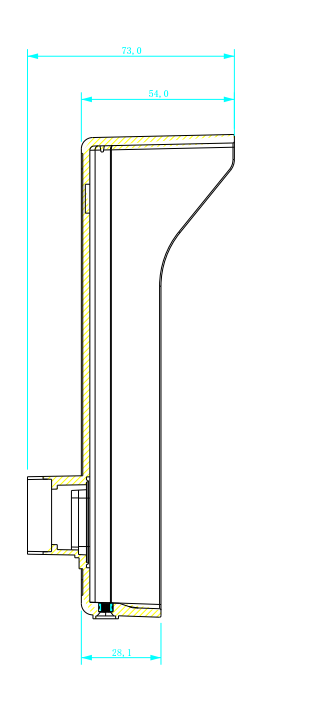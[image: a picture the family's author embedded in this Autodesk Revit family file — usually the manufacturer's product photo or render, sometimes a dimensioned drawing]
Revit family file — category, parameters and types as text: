
# Revit family: CR-02BD
name_source: partatom
category: Устройства связи
units: mm (PartAtom-declared; Revit-internal decimal feet)

## family parameters
Всегда вертикально = Нет
На основе рабочей плоскости = Да
Общий = Да
При загрузке вырезать с полостями = Нет
Размер круглого соединителя = Использовать диаметр
Сохранять ориентацию аннотаций = Нет
Тип детали = Нормальный
Точка принадлежности помещению = Нет

## types (1)
- CR-02BD
    ADSK_URL документации изделия = -
    ADSK_URL страницы изделия = https://www.bas-ip.ru
    ADSK_Версия Revit = Revit 2020
    ADSK_Единица измерения = шт
    ADSK_Завод-изготовитель = BAS-IP
    ADSK_Классификация нагрузок = Считыватель со встроенным контроллером
    ADSK_Количество фаз = 1
    ADSK_Коэффициент мощности = 0.9
    ADSK_Марка = CR-02BD
    ADSK_Наименование = Считыватель со встроенным контроллером CR-02BD
    ADSK_Наименование краткое = CR-02BD
    ADSK_Напряжение = 12 В
    ADSK_Номинальная мощность = 6 Вт
    ADSK_Полная мощность = 6 В·А
    ADSK_Размер_Длина = 159 мм
    ADSK_Размер_Толщина = 48 мм
    ADSK_Размер_Ширина = 99 мм
    BIM library = https://bimlib.ru
    URL = https://www.bas-ip.ru
    Возможность подключения дополнительного считывателя = Нет
    Группа модели = Считыватель со встроенным контроллером CR-02BD
    Допустимая влажность при эксплуатации = до 93%
    Звуковой сигнал открытия двери = Есть
    Изготовитель = BAS-IP
    Изображение типоразмера = <Нет>
    Интеграция со СКУД = Выход WIEGAND-26, 32, 34, 37, 40, 42, 56, 58, 64 бит
    Интерфейс подключения для ПО управления, ПО учета и статистики и ПО конфигурирования = RJ45 Ethernet
    Используемые протоколы работы в сети Ethernet = TCP/IP
    Класс защищенности = IP65
    Количество идентификаторов в памяти панели = 20 000
    Количество карт администратора = 1
    Корпус = Металлический сплав с высоким уровнем антивандальности и коррозионной стойкости (На лицевой панели – пластиковая декоративная накладка)
    Материал корпуса = Материал серый
    Описание = Считыватель со встроенным контроллером CR-02BD - Внешний сетевой считыватель бесконтактных карт и брелоков со встроенным контроллером и поддержкой технологии UKEY: считывание карт, брелоков и мобильных идентификаторов по стандартам Mifare® Plus и Mifare® Classic, Bluetooth, NFC. С помощью внешнего сетевого считывателя бесконтактных карт BAS-IP CR-02BD можно считывать бесконтактные карты, брелоки, а также мобильные идентификаторы с мобильных устройств
    Отметка по умолчанию = 0 мм
    Питание = PoE, +12 В (+12% -6%)
    Подключение датчика двери = Есть
    Подключение кнопки выхода = Есть
    Потребление питания = 6,0 Вт, в режиме ожидания – 2,5 Вт
    Размер = 99×159×48 мм
    Размер кронштейна = 94x 156x 59 мм
    Стандарт используемых карт и брелоков = UKEY (EM-Marin/ MIFARE®/NFC/Bluetooth)
    Температурный режим = -40 ... +65 °С
    Тип подключаемых замков = Электромеханические / электромагнитные
    Цветовое решение = Gold, Silver, Black
